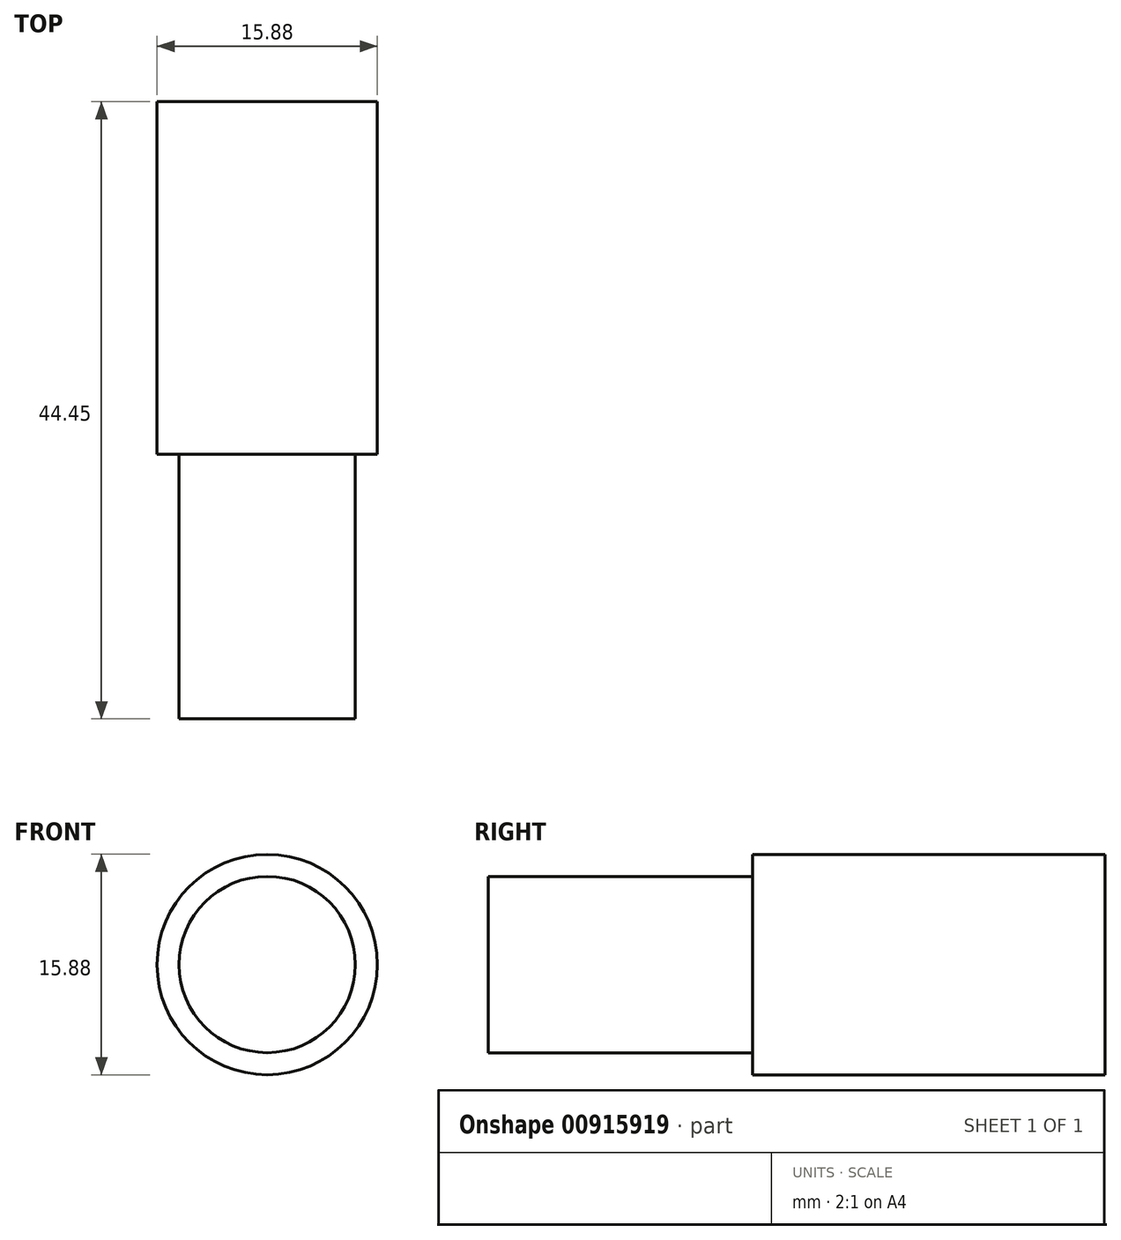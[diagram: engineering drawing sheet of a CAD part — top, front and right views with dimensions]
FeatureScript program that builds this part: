
annotation { "Feature Type Name" : "Feature", "Feature Type Description" : "" }
export const myFeature = defineFeature(function(context is Context, id is Id, definition is map)
    precondition{}
    {
        {
            var Q0;
            Q0=qCreatedBy(makeId("Front.planeOp"),FACE);
            var sketch = newSketch(context, id + "F0", { "sketchPlane" : qUnion([Q0])});
            skCircle(sketch, "E0", {"center": v(0, 0) * mm, "radius": 7.94 * mm});
            skSolve(sketch);
        }
        {
            var Q0;
            Q0=makeQuery(id+"F0.imprint","IMPRINT",FACE,{"disambiguationData":[TD([[makeQuery(id+"F0.imprint","IMPRINT",EDGE,{"derivedFrom":sQuery(id+"F0.wireOp",EDGE,"E0")}),1.0]])]});
            extrude(context, id + "F1", {"entities" : qUnion([Q0]), "oppositeDirection" : true, "depth" : 25.4 * mm, "offsetDistance" : 25.4 * mm});
        }
        {
            var Q0;
            Q0=makeQuery(id+"F1.opExtrude","CAP_FACE",FACE,{"disambiguationData":[OSD([sQuery(id+"F0.wireOp",EDGE,"E0")])],"isStart":true});
            var sketch = newSketch(context, id + "F2", { "sketchPlane" : qUnion([Q0])});
            skCircle(sketch, "E1", {"center": v(0, 0) * mm, "radius": 6.35 * mm});
            skSolve(sketch);
        }
        {
            var Q0;
            Q0=makeQuery(id+"F2.imprint","IMPRINT",FACE,{"disambiguationData":[TD([[makeQuery(id+"F2.imprint","IMPRINT",EDGE,{"derivedFrom":sQuery(id+"F2.wireOp",EDGE,"E1")}),1.0]])]});
            extrude(context, id + "F3", {"entities" : qUnion([Q0]), "depth" : 19.05 * mm, "offsetDistance" : 25.4 * mm});
        }
    });
